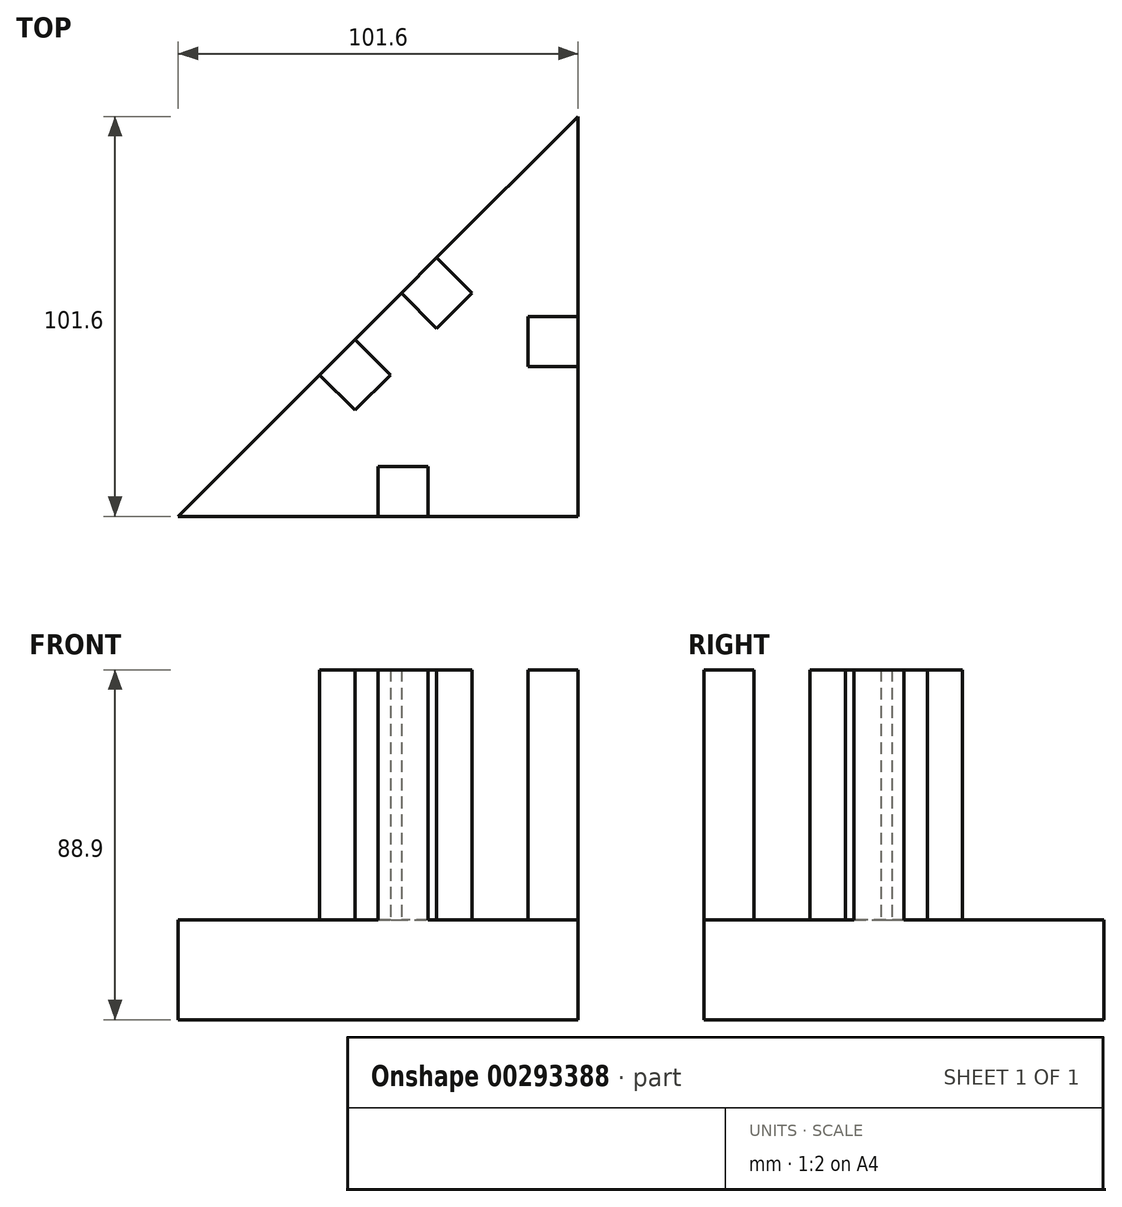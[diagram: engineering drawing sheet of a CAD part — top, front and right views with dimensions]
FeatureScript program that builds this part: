
annotation { "Feature Type Name" : "Feature", "Feature Type Description" : "" }
export const myFeature = defineFeature(function(context is Context, id is Id, definition is map)
    precondition{}
    {
        {
            var Q0;
            Q0=qCreatedBy(makeId("Top.planeOp"),FACE);
            var sketch = newSketch(context, id + "F0", { "sketchPlane" : qUnion([Q0])});
            skLineSegment(sketch, "E0.top", {"start": v(50.8, -50.8) * mm, "end": v(-50.8, -50.8) * mm});
            skLineSegment(sketch, "E0.left", {"start": v(50.8, 50.8) * mm, "end": v(50.8, -50.8) * mm});
            skPoint(sketch, "E0.middle", {"position": v(0, 0) * mm});
            skLineSegment(sketch, "E1", {"start": v(-50.8, -50.8) * mm, "end": v(50.8, 50.8) * mm});
            skLineSegment(sketch, "E2", {"start": v(-50.8, -50.8) * mm, "end": v(0, -50.8) * mm});
            skLineSegment(sketch, "E3", {"start": v(0, -50.8) * mm, "end": v(0, -38.1) * mm});
            skLineSegment(sketch, "E4", {"start": v(0, -38.1) * mm, "end": v(12.7, -38.1) * mm});
            skLineSegment(sketch, "E5", {"start": v(12.7, -38.1) * mm, "end": v(12.7, -50.8) * mm});
            skLineSegment(sketch, "E6", {"start": v(50.8, 50.8) * mm, "end": v(50.8, 0) * mm});
            skLineSegment(sketch, "E7", {"start": v(50.8, 0) * mm, "end": v(38.1, 0) * mm});
            skLineSegment(sketch, "E8", {"start": v(38.1, 0) * mm, "end": v(38.1, -12.7) * mm});
            skLineSegment(sketch, "E9", {"start": v(38.1, -12.7) * mm, "end": v(50.8, -12.7) * mm});
            skLineSegment(sketch, "E10", {"start": v(-50.8, -50.8) * mm, "end": v(-14.88, -14.88) * mm});
            skLineSegment(sketch, "E11", {"start": v(-14.88, -14.88) * mm, "end": v(-5.9, -23.86) * mm});
            skLineSegment(sketch, "E12", {"start": v(-5.9, -23.86) * mm, "end": v(3.08, -14.88) * mm});
            skLineSegment(sketch, "E13", {"start": v(3.08, -14.88) * mm, "end": v(-5.9, -5.9) * mm});
            skLineSegment(sketch, "E14", {"start": v(50.8, 50.8) * mm, "end": v(14.88, 14.88) * mm});
            skLineSegment(sketch, "E15", {"start": v(14.88, 14.88) * mm, "end": v(23.86, 5.9) * mm});
            skLineSegment(sketch, "E16", {"start": v(23.86, 5.9) * mm, "end": v(14.88, -3.08) * mm});
            skLineSegment(sketch, "E17", {"start": v(14.88, -3.08) * mm, "end": v(5.9, 5.9) * mm});
            skSolve(sketch);
        }
        {
            var Q0;
            Q0=makeQuery(id+"F0.imprint","IMPRINT",FACE,{"disambiguationData":[TD([[makeQuery(id+"F0.imprint","IMPRINT",EDGE,{"derivedFrom":sQuery(id+"F0.wireOp",EDGE,"E2")}),1.0]])]});
            var Q1;
            Q1 = qSketchRegion(id + "F0", true);
            extrude(context, id + "F1", {"entities" : qUnion([Q0, Q1]), "depth" : 25.4 * mm});
        }
        {
            var Q0;
            Q0=makeQuery(id+"F1.opExtrude","CAP_FACE",FACE,{"disambiguationData":[OSD([sQuery(id+"F0.wireOp",EDGE,"E0.top"),sQuery(id+"F0.wireOp",EDGE,"E0.left"),sQuery(id+"F0.wireOp",EDGE,"E1"),sQuery(id+"F0.wireOp",EDGE,"E2"),sQuery(id+"F0.wireOp",EDGE,"E6"),sQuery(id+"F0.wireOp",EDGE,"E10"),sQuery(id+"F0.wireOp",EDGE,"E14")])],"isStart":false});
            var sketch = newSketch(context, id + "F2", { "sketchPlane" : qUnion([Q0])});
            skLineSegment(sketch, "E18", {"start": v(-50.8, -50.8) * mm, "end": v(0, -50.8) * mm});
            skLineSegment(sketch, "E19", {"start": v(0, -50.8) * mm, "end": v(0, -38.1) * mm});
            skLineSegment(sketch, "E20", {"start": v(0, -38.1) * mm, "end": v(12.7, -38.1) * mm});
            skLineSegment(sketch, "E21", {"start": v(12.7, -38.1) * mm, "end": v(12.7, -50.8) * mm});
            skLineSegment(sketch, "E22", {"start": v(50.8, 50.8) * mm, "end": v(50.8, 0) * mm});
            skLineSegment(sketch, "E23", {"start": v(50.8, 0) * mm, "end": v(38.1, 0) * mm});
            skLineSegment(sketch, "E24", {"start": v(38.1, 0) * mm, "end": v(38.1, -12.7) * mm});
            skLineSegment(sketch, "E25", {"start": v(38.1, -12.7) * mm, "end": v(50.8, -12.7) * mm});
            skLineSegment(sketch, "E26", {"start": v(-50.8, -50.8) * mm, "end": v(-14.88, -14.88) * mm});
            skLineSegment(sketch, "E27", {"start": v(-14.88, -14.88) * mm, "end": v(-5.9, -23.86) * mm});
            skLineSegment(sketch, "E28", {"start": v(-5.9, -23.86) * mm, "end": v(3.08, -14.88) * mm});
            skLineSegment(sketch, "E29", {"start": v(3.08, -14.88) * mm, "end": v(-5.9, -5.9) * mm});
            skLineSegment(sketch, "E30", {"start": v(50.8, 50.8) * mm, "end": v(14.88, 14.88) * mm});
            skLineSegment(sketch, "E31", {"start": v(14.88, 14.88) * mm, "end": v(23.86, 5.9) * mm});
            skLineSegment(sketch, "E32", {"start": v(23.86, 5.9) * mm, "end": v(14.88, -3.08) * mm});
            skLineSegment(sketch, "E33", {"start": v(14.88, -3.08) * mm, "end": v(5.9, 5.9) * mm});
            skSolve(sketch);
        }
        {
            var Q0;
            {var subQ0=sQuery(id+"F2.wireOp",EDGE,"E23");Q0=makeQuery(id+"F2.imprint","IMPRINT",FACE,{"disambiguationData":[TD([[makeQuery(id+"F2.imprint","IMPRINT",EDGE,{"derivedFrom":subQ0}),1.0]])]});}
            var Q1;
            {var subQ0=sQuery(id+"F2.wireOp",EDGE,"E31");Q1=makeQuery(id+"F2.imprint","IMPRINT",FACE,{"disambiguationData":[TD([[makeQuery(id+"F2.imprint","IMPRINT",EDGE,{"derivedFrom":subQ0}),-1.0]])]});}
            var Q2;
            {var subQ0=sQuery(id+"F2.wireOp",EDGE,"E27");Q2=makeQuery(id+"F2.imprint","IMPRINT",FACE,{"disambiguationData":[TD([[makeQuery(id+"F2.imprint","IMPRINT",EDGE,{"derivedFrom":subQ0}),1.0]])]});}
            var Q3;
            {var subQ0=sQuery(id+"F2.wireOp",EDGE,"E19");Q3=makeQuery(id+"F2.imprint","IMPRINT",FACE,{"disambiguationData":[TD([[makeQuery(id+"F2.imprint","IMPRINT",EDGE,{"derivedFrom":subQ0}),-1.0]])]});}
            extrude(context, id + "F3", {"entities" : qUnion([Q0, Q1, Q2, Q3]), "operationType" : NewBodyOperationType.ADD, "depth" : 63.5 * mm});
        }
    });
